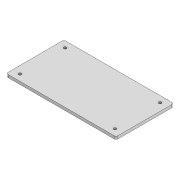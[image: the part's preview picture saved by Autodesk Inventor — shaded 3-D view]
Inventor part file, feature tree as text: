
AUTODESK INVENTOR PART (.ipt)
format: ipt  version: 2020 (Build 240168000, 168)  size: 152,064 bytes
history: native  units: mm
features: extrude x3, sketch x3, fillet x1
ambient origin geometry x8: Origin, YZ Plane, XZ Plane, XY Plane, X Axis, Y Axis, Z Axis, Center Point
bodies: Solid1 (feature_tree)
feature tree (7):
  extrude  "Extrusion1"  Depth=140.0mm
  extrude  "Extrusion2"  Depth=48.5mm
  extrude  "Extrusion3"  Depth=3.0mm
  fillet  "Fillet1"  Radius=3.0mm
  sketch  "Sketch1"  dims[d0=150.0mm d1=140.0mm]
  sketch  "Sketch2"  dims[d2=102.0mm d3=48.5mm]
  sketch  "Sketch3"  dims[d4=3.0mm d5=3.0mm d6=3.0mm d7=3.0mm d8=3.0mm d9=0.0mm d10=40.0mm d11=3.0mm d12=40.0mm d13=3.0mm d14=5.0mm d15=0.0mm d16=118.0mm d17=62.0mm d18=10.0mm d19=0.0mm d20=2.0mm]
